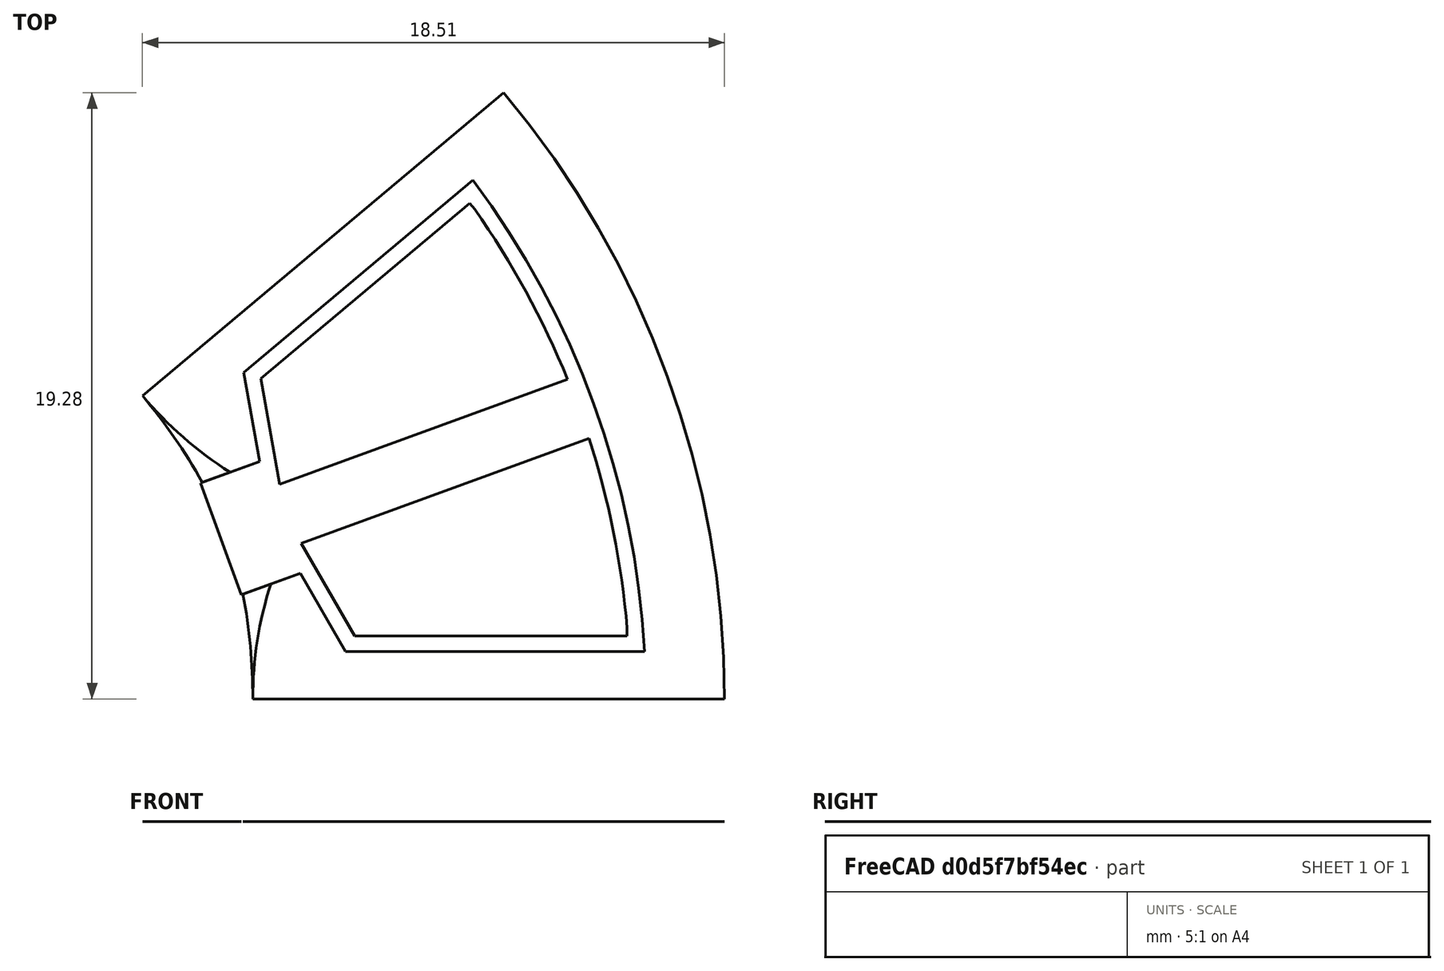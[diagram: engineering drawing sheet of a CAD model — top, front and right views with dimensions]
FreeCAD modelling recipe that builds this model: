
FCSTD DOCUMENT  (FreeCAD 0.18R4 (GitTag))
Label: StatorIRRoundBack
License: All rights reserved
LicenseURL: http://en.wikipedia.org/wiki/All_rights_reserved
objects: Sketcher::SketchObject×9, Surface::Filling×5, PartDesign::Body×2, Spreadsheet::Sheet×1
note: 16 computed .brp shape members not serialized (recipe doc carries the construction recipe); baked Part::Feature solids carry a one-line shape summary decoded from their .brp

FEATURE [Spreadsheet::Sheet] Spreadsheet  label="Variables"
  cells = A2=slotNumber; B2(slotNumber)=9; A3=outerDiameter; B3(outerDiameter)=60; A4=innerDiameter; B4(innerDiameter)=30; A5=stackLength; B5(stackLength)=20; A6=stackingFactor; B6(stackingFactor)=0.95; A7=cuttingThickness; B7(cuttingThickness)=0.1; A8=skewAngle; B8(skewAngle)=0; A9=segmentAngle; B9(segmentAngle)==360 / slotNumber; A10=tipHeightReduction; B10(tipHeightReduction)=3; A11=toothThickness; B11(toothThickness)=3; A12=yokeThickness; B12(yokeThickness)=2.5; A13=tipHeight; B13(tipHeight)=2; A14=tipAngle; B14(tipAngle)=120; A15=openingLeft; B15(openingLeft)=1.9; A16=openingRight; B16(openingRight)=1.9; A17=slotIsolation; B17(slotIsolation)=0.5; A18=windingAngle; B18(windingAngle)=35; A19=heightRatio; B19(heightRatio)=45; A20=roundingRadii; B20(roundingRadii)=0.2; A21=backWidth; B21(backWidth)=3; A22=backAngle; B22(backAngle)=90; A23=phaseSeparation; B23(phaseSeparation)=2; A24=axialOverhang; B24(axialOverhang)=1.2; A25=axialHeight; B25(axialHeight)=3
FEATURE [Sketcher::SketchObject] Sketch003  label="StatorSketch1"
  MapMode = 5
  Support = -> [XY_Plane]
  expr: Constraints[22] = Variables.openingLeft
  expr: Constraints[54] = Variables.tipHeight
  expr: Constraints[11] = Variables.innerDiameter / 2
  expr: Constraints[5] = Variables.segmentAngle
  expr: Constraints[37] = Variables.tipAngle
  expr: Constraints[30] = Variables.tipHeight
  expr: Constraints[28] = Variables.openingRight
  expr: Constraints[51] = Variables.outerDiameter / 2 - Variables.yokeThickness
  expr: Constraints[18] = Variables.segmentAngle / 2
  expr: Constraints[32] = Variables.tipHeight * (1 - Variables.tipHeightReduction / 100)
  expr: Constraints[6] = Variables.outerDiameter / 2
  expr: Constraints[48] = Variables.tipAngle
  expr: Constraints[47] = Variables.tipHeight * (1 - Variables.tipHeightReduction / 100)
  expr: Constraints[42] = Variables.toothThickness / 2
  sketch-geometry (24):
    g0: LineSegment [constr] StartX=0 StartY=0 StartZ=0 EndX=22.9813 EndY=19.2836 EndZ=0
    g1: LineSegment [constr] StartX=0 StartY=0 StartZ=0 EndX=30 EndY=0 EndZ=0
    g2: ArcOfCircle CenterX=0 CenterY=0 CenterZ=0 NormalX=0 NormalY=0 NormalZ=1 AngleXU=0 Radius=30 StartAngle=0 EndAngle=0.698132
    g3: ArcOfCircle [constr] CenterX=0 CenterY=0 CenterZ=0 NormalX=0 NormalY=0 NormalZ=1 AngleXU=0 Radius=15 StartAngle=0 EndAngle=0.698132
    g4: LineSegment [constr] StartX=13.3338 StartY=6.87098 StartZ=0 EndX=27.4859 EndY=12.0219 EndZ=0
    g5: LineSegment [constr] StartX=14.6308 StartY=3.30731 StartZ=0 EndX=28.7829 EndY=8.45826 EndZ=0
    g6: LineSegment [constr] StartX=28.1908 StartY=10.2606 StartZ=0 EndX=14.0954 EndY=5.1303 EndZ=0
    g7: LineSegment [constr] StartX=0 StartY=0 StartZ=0 EndX=14.0954 EndY=5.1303 EndZ=0
    g8: LineSegment [constr] StartX=13.3338 StartY=6.87098 StartZ=0 EndX=14.0954 EndY=5.1303 EndZ=0
    g9: LineSegment [constr] StartX=14.0954 StartY=5.1303 StartZ=0 EndX=14.6308 EndY=3.30731 EndZ=0
    g10: LineSegment [constr] StartX=13.3902 StartY=6.8915 StartZ=0 EndX=15.2132 EndY=7.55502 EndZ=0
    g11: LineSegment StartX=13.3902 StartY=6.8915 StartZ=0 EndX=15.2132 EndY=7.55502 EndZ=0
    g12: LineSegment StartX=15.2132 StartY=7.55502 StartZ=0 EndX=14.7136 EndY=10.3881 EndZ=0
    g13: LineSegment StartX=14.7136 StartY=10.3881 StartZ=0 EndX=21.999 EndY=16.5013 EndZ=0
    g14: LineSegment [constr] StartX=14.7136 StartY=10.3881 StartZ=0 EndX=13.7494 EndY=11.5371 EndZ=0
    g15: LineSegment StartX=27.4591 StartY=1.5 StartZ=0 EndX=17.9486 EndY=1.5 EndZ=0
    g16: LineSegment StartX=17.9486 StartY=1.5 StartZ=0 EndX=16.5102 EndY=3.99135 EndZ=0
    g17: LineSegment StartX=16.5102 StartY=3.99135 StartZ=0 EndX=14.6872 EndY=3.32784 EndZ=0
    g18: LineSegment [constr] StartX=27.4591 StartY=1.5 StartZ=0 EndX=27.4591 EndY=0 EndZ=0
    g19: LineSegment StartX=11.4907 StartY=9.64181 StartZ=0 EndX=22.9813 EndY=19.2836 EndZ=0
    g20: LineSegment StartX=30 StartY=0 StartZ=0 EndX=15 EndY=0 EndZ=0
    g21: ArcOfCircle CenterX=-2.86017 CenterY=0 CenterZ=0 NormalX=0 NormalY=0 NormalZ=1 AngleXU=0 Radius=17.8602 StartAngle=0 EndAngle=0.187423
    g22: ArcOfCircle CenterX=-2.19102 CenterY=-1.83848 CenterZ=0 NormalX=0 NormalY=0 NormalZ=1 AngleXU=0 Radius=17.8602 StartAngle=0.510709 EndAngle=0.698132
    g23: ArcOfCircle CenterX=0 CenterY=0 CenterZ=0 NormalX=0 NormalY=0 NormalZ=1 AngleXU=0 Radius=27.5 StartAngle=0.0545725 EndAngle=0.643559
  constraints (69):
    c: Angle(g-1,g1) = 0
    c: Coincident(g0,g-1)
    c: Coincident(g1,g-1)
    c: Coincident(g2,g-1)
    c: Coincident(g2,g0)
    c: Angle(g1,g0) = 0.698132
    c: Radius(g2) = 30
    c: Coincident(g2,g1)
    c: Coincident(g3,g-1)
    c: PointOnObject(g3,g1)
    c: PointOnObject(g3,g0)
    c: Radius(g3) = 15
    c: PointOnObject(g4,g3)
    c: PointOnObject(g4,g2)
    c: PointOnObject(g5,g3)
    c: PointOnObject(g5,g2)
    c: PointOnObject(g6,g2)
    c: PointOnObject(g6,g3)
    c: Angle(g1,g6) = 0.349066
    c: Coincident(g7,g-1)
    c: Coincident(g7,g6)
    c: Coincident(g8,g4)
    c: Distance(g8) = 1.9
    c: Coincident(g8,g6)
    c: Parallel(g4,g6)
    c: Parallel(g5,g6)
    c: Coincident(g9,g6)
    c: Coincident(g9,g5)
    c: Distance(g9) = 1.9
    c: PointOnObject(g10,g4)
    c: Distance(g4,g10) = 2
    c: Angle(g4,g10) = 3.14159
    c: Distance(g10,g10) = 1.94
    c: Coincident(g11,g10)
    c: Coincident(g12,g11)
    c: Coincident(g13,g12)
    c: Coincident(g11,g10)
    c: Angle(g12,g13) = 2.0944
    c: Parallel(g0,g13)
    c: Coincident(g14,g12)
    c: PointOnObject(g14,g0)
    c: Angle(g13,g14) = 1.5708
    c: Distance(g14) = 1.5
    c: Coincident(g16,g15)
    c: PointOnObject(g16,g5)
    c: Coincident(g17,g16)
    c: PointOnObject(g17,g5)
    c: Distance(g17) = 1.94
    c: Angle(g15,g16) = 2.0944
    c: Parallel(g15,g1)
    c: Symmetric(g23,g23,g6)
    c: Distance(g-1,g23) = 27.5
    c: PointOnObject(g18,g1)
    c: Vertical(g18)
    c: Distance(g5,g16) = 2
    c: Coincident(g19,g3)
    c: Coincident(g19,g0)
    c: Coincident(g20,g2)
    c: Coincident(g20,g3)
    c: PointOnObject(g21,g-1)
    c: Coincident(g21,g17)
    c: Coincident(g21,g20)
    c: PointOnObject(g22,g0)
    c: Coincident(g22,g11)
    c: Coincident(g22,g19)
    c: Coincident(g23,g2)
    c: Coincident(g23,g13)
    c: Coincident(g15,g23)
    c: Coincident(g18,g15)
FEATURE [Sketcher::SketchObject] Sketch  label="StatorStack"
  MapMode = 5
  Support = -> [XY_Plane001]
  expr: Constraints[20] = Variables.innerDiameter / 2
  expr: Constraints[10] = Variables.outerDiameter / 2
  expr: Constraints[9] = Variables.innerDiameter / 2
  expr: Constraints[8] = Variables.stackLength
  sketch-geometry (8):
    g0: LineSegment StartX=-10 StartY=15 StartZ=0 EndX=10 EndY=15 EndZ=0
    g1: LineSegment StartX=10 StartY=15 StartZ=0 EndX=10 EndY=30 EndZ=0
    g2: LineSegment StartX=10 StartY=30 StartZ=0 EndX=-10 EndY=30 EndZ=0
    g3: LineSegment StartX=-10 StartY=30 StartZ=0 EndX=-10 EndY=15 EndZ=0
    g4: LineSegment StartX=-10 StartY=-15 StartZ=0 EndX=10 EndY=-15 EndZ=0
    g5: LineSegment StartX=10 StartY=-15 StartZ=0 EndX=10 EndY=-30 EndZ=0
    g6: LineSegment StartX=10 StartY=-30 StartZ=0 EndX=-10 EndY=-30 EndZ=0
    g7: LineSegment StartX=-10 StartY=-30 StartZ=0 EndX=-10 EndY=-15 EndZ=0
  constraints (22):
    c: Coincident(g0,g1)
    c: Coincident(g1,g2)
    c: Coincident(g2,g3)
    c: Coincident(g3,g0)
    c: Horizontal(g2)
    c: Vertical(g1)
    c: Vertical(g3)
    c: Symmetric(g0,g0,g-2)
    c: DistanceX(g0,g0) = 20
    c: DistanceY(g-1,g0) = 15
    c: DistanceY(g-1,g1) = 30
    c: Coincident(g4,g5)
    c: Coincident(g5,g6)
    c: Coincident(g6,g7)
    c: Coincident(g7,g4)
    c: Horizontal(g6)
    c: Vertical(g5)
    c: Vertical(g7)
    c: Equal(g4,g0)
    c: Symmetric(g4,g4,g-2)
    c: DistanceY(g4,g-1) = 15
    c: Equal(g7,g3)
FEATURE [Sketcher::SketchObject] Sketch008  label="SlotSketch"
  MapMode = 5
  Support = -> [XY_Plane]
  expr: Constraints[63] = Variables.outerDiameter / 2 - Variables.yokeThickness
  expr: Constraints[43] = Variables.toothThickness / 2
  expr: Constraints[34] = Variables.toothThickness / 2
  expr: Constraints[40] = Variables.outerDiameter / 2 - Variables.yokeThickness
  expr: Constraints[21] = Variables.openingLeft
  expr: Constraints[44] = Variables.tipHeight
  expr: Constraints[57] = Variables.backWidth
  expr: Constraints[5] = Variables.segmentAngle
  expr: Constraints[29] = Variables.tipAngle
  expr: Constraints[27] = Variables.openingRight
  expr: Constraints[62] = Variables.segmentAngle / 2
  expr: Constraints[6] = Variables.outerDiameter / 2
  expr: Constraints[37] = Variables.tipAngle
  expr: Constraints[11] = Variables.innerDiameter / 2
  sketch-geometry (23):
    g0: LineSegment [constr] StartX=0 StartY=0 StartZ=0 EndX=22.9813 EndY=19.2836 EndZ=0
    g1: LineSegment [constr] StartX=0 StartY=0 StartZ=0 EndX=30 EndY=0 EndZ=0
    g2: ArcOfCircle [constr] CenterX=0 CenterY=0 CenterZ=0 NormalX=0 NormalY=0 NormalZ=1 AngleXU=0 Radius=30 StartAngle=0 EndAngle=0.698132
    g3: ArcOfCircle [constr] CenterX=0 CenterY=0 CenterZ=0 NormalX=0 NormalY=0 NormalZ=1 AngleXU=0 Radius=15 StartAngle=0 EndAngle=0.698132
    g4: LineSegment [constr] StartX=13.3338 StartY=6.87098 StartZ=0 EndX=27.4859 EndY=12.0219 EndZ=0
    g5: LineSegment [constr] StartX=14.6308 StartY=3.30731 StartZ=0 EndX=28.7829 EndY=8.45826 EndZ=0
    g6: LineSegment [constr] StartX=28.1908 StartY=10.2606 StartZ=0 EndX=14.0954 EndY=5.1303 EndZ=0
    g7: LineSegment [constr] StartX=0 StartY=0 StartZ=0 EndX=14.0954 EndY=5.1303 EndZ=0
    g8: LineSegment [constr] StartX=13.3338 StartY=6.87098 StartZ=0 EndX=14.0954 EndY=5.1303 EndZ=0
    g9: LineSegment [constr] StartX=14.0954 StartY=5.1303 StartZ=0 EndX=14.6308 EndY=3.30731 EndZ=0
    g10: LineSegment StartX=15.2132 StartY=7.55502 StartZ=0 EndX=14.7136 EndY=10.3881 EndZ=0
    g11: LineSegment StartX=14.7136 StartY=10.3881 StartZ=0 EndX=21.999 EndY=16.5013 EndZ=0
    g12: LineSegment [constr] StartX=14.7136 StartY=10.3881 StartZ=0 EndX=13.7494 EndY=11.5371 EndZ=0
    g13: LineSegment [constr] StartX=25.29 StartY=10.8011 StartZ=0 EndX=26.3161 EndY=7.98201 EndZ=0
    g14: LineSegment StartX=27.4591 StartY=1.5 StartZ=0 EndX=17.9486 EndY=1.5 EndZ=0
    g15: LineSegment StartX=17.9486 StartY=1.5 StartZ=0 EndX=16.5102 EndY=3.99135 EndZ=0
    g16: LineSegment [constr] StartX=27.4591 StartY=1.5 StartZ=0 EndX=27.4591 EndY=0 EndZ=0
    g17: LineSegment [constr] StartX=11.4907 StartY=9.64181 StartZ=0 EndX=22.9813 EndY=19.2836 EndZ=0
    g18: LineSegment [constr] StartX=30 StartY=0 StartZ=0 EndX=15 EndY=0 EndZ=0
    g19: LineSegment StartX=13.3338 StartY=6.87098 StartZ=0 EndX=14.6308 EndY=3.30731 EndZ=0
    g20: LineSegment StartX=13.3338 StartY=6.87098 StartZ=0 EndX=15.2132 EndY=7.55502 EndZ=0
    g21: LineSegment StartX=14.6308 StartY=3.30731 StartZ=0 EndX=16.5102 EndY=3.99135 EndZ=0
    g22: ArcOfCircle CenterX=0 CenterY=0 CenterZ=0 NormalX=0 NormalY=0 NormalZ=1 AngleXU=0 Radius=27.5 StartAngle=0.0545725 EndAngle=0.643559
  constraints (64):
    c: Angle(g-1,g1) = 0
    c: Coincident(g0,g-1)
    c: Coincident(g1,g-1)
    c: Coincident(g2,g-1)
    c: Coincident(g2,g0)
    c: Angle(g1,g0) = 0.698132
    c: Radius(g2) = 30
    c: Coincident(g2,g1)
    c: Coincident(g3,g-1)
    c: PointOnObject(g3,g1)
    c: PointOnObject(g3,g0)
    c: Radius(g3) = 15
    c: PointOnObject(g4,g3)
    c: PointOnObject(g4,g2)
    c: PointOnObject(g5,g3)
    c: PointOnObject(g5,g2)
    c: PointOnObject(g6,g2)
    c: PointOnObject(g6,g3)
    c: Coincident(g7,g-1)
    c: Coincident(g7,g6)
    c: Coincident(g8,g4)
    c: Distance(g8) = 1.9
    c: Coincident(g8,g6)
    c: Parallel(g4,g6)
    c: Parallel(g5,g6)
    c: Coincident(g9,g6)
    c: Coincident(g9,g5)
    c: Distance(g9) = 1.9
    c: Coincident(g11,g10)
    c: Angle(g10,g11) = 2.0944
    c: Parallel(g0,g11)
    c: Coincident(g12,g10)
    c: PointOnObject(g12,g0)
    c: Angle(g11,g12) = 1.5708
    c: Distance(g12) = 1.5
    c: Coincident(g15,g14)
    c: PointOnObject(g15,g5)
    c: Angle(g14,g15) = 2.0944
    c: Parallel(g14,g1)
    c: Symmetric(g13,g13,g6)
    c: Distance(g-1,g13) = 27.5
    c: PointOnObject(g16,g1)
    c: Vertical(g16)
    c: DistanceY(g16,g16) = 1.5
    c: Distance(g5,g15) = 2
    c: Coincident(g17,g3)
    c: Coincident(g17,g0)
    c: Coincident(g18,g2)
    c: Coincident(g18,g3)
    c: Symmetric(g15,g10,g6)
    c: Coincident(g19,g4)
    c: Coincident(g19,g5)
    c: Coincident(g20,g19)
    c: Coincident(g20,g10)
    c: Coincident(g21,g19)
    c: Coincident(g21,g15)
    c: Coincident(g22,g-1)
    c: Distance(g13) = 3
    c: Coincident(g22,g11)
    c: Coincident(g22,g14)
    c: Coincident(g14,g16)
    c: Parallel(g7,g6)
    c: Angle(g1,g7) = 0.349066
    c: Radius(g22) = 27.5
FEATURE [Surface::Filling] Surface  label="SlotSketch_Surface"
  Anisotropy = false
  BoundaryEdges = -> [Sketch008]
  BoundaryOrder = [0,0,0,0,0,0,0,0]
  Degree = 3
  Iterations = 2
  MaximumDegree = 8
  MaximumSegments = 9
  PointsOnCurve = 15
  TolAngular = 0.01
  TolCurvature = 0.1
  Tolerance2d = 1e-05
  Tolerance3d = 0.0001
FEATURE [Surface::Filling] Surface002  label="StatorSketch1_Surface"
  Anisotropy = false
  BoundaryEdges = -> [Sketch003]
  BoundaryOrder = [0,0,0,0,0,0,0,0,0,0,0,0]
  Degree = 3
  Iterations = 2
  MaximumDegree = 8
  MaximumSegments = 9
  PointsOnCurve = 15
  TolAngular = 0.01
  TolCurvature = 0.1
  Tolerance2d = 1e-05
  Tolerance3d = 0.0001
FEATURE [Sketcher::SketchObject] Sketch010  label="ToothLine"
  ExternalGeometry = -> [Sketch008]
  MapMode = 5
  Support = -> [XY_Plane]
  expr: Constraints[0] = Variables.toothThickness
  sketch-geometry (1):
    g0: LineSegment StartX=18.3563 StartY=13.4447 StartZ=0 EndX=16.428 EndY=15.7428 EndZ=0
  constraints (3):
    c: Distance(g0) = 3
    c: Symmetric(g-3,g-3,g0)
    c: Angle(g-3,g0) = 1.5708
FEATURE [Sketcher::SketchObject] Sketch011  label="YokeLine"
  ExternalGeometry = -> [Sketch008]
  MapMode = 5
  Support = -> [XY_Plane]
  expr: Constraints[0] = Variables.yokeThickness
  sketch-geometry (3):
    g0: LineSegment StartX=25.8415 StartY=9.40555 StartZ=0 EndX=28.1908 EndY=10.2606 EndZ=0
    g1: LineSegment [constr] StartX=21.999 StartY=16.5013 StartZ=0 EndX=27.4591 EndY=1.5 EndZ=0
    g2: LineSegment [constr] StartX=25.8415 StartY=9.40555 StartZ=0 EndX=24.7291 EndY=9.00064 EndZ=0
  constraints (8):
    c: Distance(g0) = 2.5
    c: PointOnObject(g0,g-3)
    c: Coincident(g1,g-3)
    c: Coincident(g1,g-3)
    c: Coincident(g2,g0)
    c: Angle(g2,g0) = 3.14159
    c: Angle(g1,g2) = 1.5708
    c: Symmetric(g1,g1,g2)
FEATURE [Sketcher::SketchObject] Sketch012  label="StatorSketch2"
  MapMode = 5
  Support = -> [XY_Plane]
  expr: Constraints[22] = Variables.openingLeft
  expr: Constraints[54] = Variables.tipHeight
  expr: Constraints[11] = Variables.innerDiameter / 2
  expr: Constraints[5] = Variables.segmentAngle
  expr: Constraints[37] = Variables.tipAngle
  expr: Constraints[30] = Variables.tipHeight
  expr: Constraints[28] = Variables.openingRight
  expr: Constraints[51] = Variables.outerDiameter / 2 - Variables.yokeThickness
  expr: Constraints[18] = Variables.segmentAngle / 2
  expr: Constraints[32] = Variables.tipHeight * (1 - Variables.tipHeightReduction / 100)
  expr: Constraints[6] = Variables.outerDiameter / 2
  expr: Constraints[48] = Variables.tipAngle
  expr: Constraints[47] = Variables.tipHeight * (1 - Variables.tipHeightReduction / 100)
  expr: Constraints[42] = Variables.toothThickness / 2
  sketch-geometry (24):
    g0: LineSegment [constr] StartX=0 StartY=0 StartZ=0 EndX=22.9813 EndY=19.2836 EndZ=0
    g1: LineSegment [constr] StartX=0 StartY=0 StartZ=0 EndX=30 EndY=0 EndZ=0
    g2: ArcOfCircle CenterX=0 CenterY=0 CenterZ=0 NormalX=0 NormalY=0 NormalZ=1 AngleXU=0 Radius=30 StartAngle=0 EndAngle=0.698132
    g3: ArcOfCircle [constr] CenterX=0 CenterY=0 CenterZ=0 NormalX=0 NormalY=0 NormalZ=1 AngleXU=0 Radius=15 StartAngle=0 EndAngle=0.698132
    g4: LineSegment [constr] StartX=13.3338 StartY=6.87098 StartZ=0 EndX=27.4859 EndY=12.0219 EndZ=0
    g5: LineSegment [constr] StartX=14.6308 StartY=3.30731 StartZ=0 EndX=28.7829 EndY=8.45826 EndZ=0
    g6: LineSegment [constr] StartX=28.1908 StartY=10.2606 StartZ=0 EndX=14.0954 EndY=5.1303 EndZ=0
    g7: LineSegment [constr] StartX=0 StartY=0 StartZ=0 EndX=14.0954 EndY=5.1303 EndZ=0
    g8: LineSegment [constr] StartX=13.3338 StartY=6.87098 StartZ=0 EndX=14.0954 EndY=5.1303 EndZ=0
    g9: LineSegment [constr] StartX=14.0954 StartY=5.1303 StartZ=0 EndX=14.6308 EndY=3.30731 EndZ=0
    g10: LineSegment [constr] StartX=14.2735 StartY=7.213 StartZ=0 EndX=15.2132 EndY=7.55502 EndZ=0
    g11: LineSegment StartX=14.2735 StartY=7.213 StartZ=0 EndX=15.2132 EndY=7.55502 EndZ=0
    g12: LineSegment StartX=15.2132 StartY=7.55502 StartZ=0 EndX=14.7136 EndY=10.3881 EndZ=0
    g13: LineSegment StartX=14.7136 StartY=10.3881 StartZ=0 EndX=21.999 EndY=16.5013 EndZ=0
    g14: LineSegment [constr] StartX=14.7136 StartY=10.3881 StartZ=0 EndX=13.7494 EndY=11.5371 EndZ=0
    g15: LineSegment StartX=27.4591 StartY=1.5 StartZ=0 EndX=17.9486 EndY=1.5 EndZ=0
    g16: LineSegment StartX=17.9486 StartY=1.5 StartZ=0 EndX=16.5102 EndY=3.99135 EndZ=0
    g17: LineSegment StartX=16.5102 StartY=3.99135 StartZ=0 EndX=15.5705 EndY=3.64933 EndZ=0
    g18: LineSegment [constr] StartX=27.4591 StartY=1.5 StartZ=0 EndX=27.4591 EndY=0 EndZ=0
    g19: LineSegment StartX=11.4907 StartY=9.64181 StartZ=0 EndX=22.9813 EndY=19.2836 EndZ=0
    g20: LineSegment StartX=30 StartY=0 StartZ=0 EndX=15 EndY=0 EndZ=0
    g21: ArcOfCircle CenterX=0 CenterY=0 CenterZ=0 NormalX=0 NormalY=0 NormalZ=1 AngleXU=0 Radius=27.5 StartAngle=0.0545725 EndAngle=0.643559
    g22: ArcOfCircle CenterX=20.6498 CenterY=17.3272 CenterZ=0 NormalX=0 NormalY=0 NormalZ=1 AngleXU=0 Radius=11.9564 StartAngle=3.83972 EndAngle=4.14989
    g23: ArcOfCircle CenterX=26.9564 CenterY=0 CenterZ=0 NormalX=0 NormalY=0 NormalZ=1 AngleXU=0 Radius=11.9564 StartAngle=2.83142 EndAngle=3.14159
  constraints (69):
    c: Angle(g-1,g1) = 0
    c: Coincident(g0,g-1)
    c: Coincident(g1,g-1)
    c: Coincident(g2,g-1)
    c: Coincident(g2,g0)
    c: Angle(g1,g0) = 0.698132
    c: Radius(g2) = 30
    c: Coincident(g2,g1)
    c: Coincident(g3,g-1)
    c: PointOnObject(g3,g1)
    c: PointOnObject(g3,g0)
    c: Radius(g3) = 15
    c: PointOnObject(g4,g3)
    c: PointOnObject(g4,g2)
    c: PointOnObject(g5,g3)
    c: PointOnObject(g5,g2)
    c: PointOnObject(g6,g2)
    c: PointOnObject(g6,g3)
    c: Angle(g1,g6) = 0.349066
    c: Coincident(g7,g-1)
    c: Coincident(g7,g6)
    c: Coincident(g8,g4)
    c: Distance(g8) = 1.9
    c: Coincident(g8,g6)
    c: Parallel(g4,g6)
    c: Parallel(g5,g6)
    c: Coincident(g9,g6)
    c: Coincident(g9,g5)
    c: Distance(g9) = 1.9
    c: PointOnObject(g10,g4)
    c: Distance(g4,g10) = 2
    c: Angle(g4,g10) = 3.14159
    c: Distance(g10,g10) = 1.94
    c: Coincident(g11,g10)
    c: Coincident(g12,g11)
    c: Coincident(g13,g12)
    c: Coincident(g11,g10)
    c: Angle(g12,g13) = 2.0944
    c: Parallel(g0,g13)
    c: Coincident(g14,g12)
    c: PointOnObject(g14,g0)
    c: Angle(g13,g14) = 1.5708
    c: Distance(g14) = 1.5
    c: Coincident(g16,g15)
    c: PointOnObject(g16,g5)
    c: Coincident(g17,g16)
    c: PointOnObject(g17,g5)
    c: Distance(g17) = 1.94
    c: Angle(g15,g16) = 2.0944
    c: Parallel(g15,g1)
    c: Symmetric(g21,g21,g6)
    c: Distance(g-1,g21) = 27.5
    c: PointOnObject(g18,g1)
    c: Vertical(g18)
    c: Distance(g5,g16) = 2
    c: Coincident(g19,g3)
    c: Coincident(g19,g0)
    c: Coincident(g20,g2)
    c: Coincident(g20,g3)
    c: Coincident(g21,g2)
    c: Coincident(g21,g13)
    c: Coincident(g15,g21)
    c: Coincident(g18,g15)
    c: PointOnObject(g22,g19)
    c: Coincident(g22,g19)
    c: Coincident(g22,g11)
    c: PointOnObject(g23,g20)
    c: Coincident(g23,g20)
    c: Coincident(g23,g17)
FEATURE [Surface::Filling] Surface001  label="StatorSketch2_Surface"
  Anisotropy = false
  BoundaryEdges = -> [Sketch012]
  BoundaryOrder = [0,0,0,0,0,0,0,0,0,0,0,0,0,0]
  Degree = 3
  Iterations = 2
  MaximumDegree = 8
  MaximumSegments = 9
  PointsOnCurve = 15
  TolAngular = 0.01
  TolCurvature = 0.1
  Tolerance2d = 1e-05
  Tolerance3d = 0.0001
FEATURE [Sketcher::SketchObject] Sketch013  label="TerminalLeftSketch"
  ExternalGeometry = -> [Sketch008]
  MapMode = 5
  Support = -> [XY_Plane]
  expr: Constraints[19] = Variables.slotIsolation
  expr: Constraints[20] = Variables.slotIsolation / 2
  expr: Constraints[15] = Variables.outerDiameter / 2 - Variables.yokeThickness - Variables.slotIsolation
  expr: Constraints[12] = Variables.phaseSeparation / 2
  sketch-geometry (9):
    g0: LineSegment StartX=22.0575 StartY=15.5713 StartZ=0 EndX=21.8968 EndY=15.7628 EndZ=0
    g1: LineSegment StartX=21.8968 StartY=15.7628 StartZ=0 EndX=15.2562 EndY=10.1906 EndZ=0
    g2: LineSegment StartX=15.2562 StartY=10.1906 StartZ=0 EndX=15.8483 EndY=6.83248 EndZ=0
    g3: LineSegment StartX=15.8483 StartY=6.83248 StartZ=0 EndX=25.0123 EndY=10.1679 EndZ=0
    g4: ArcOfCircle CenterX=0 CenterY=0 CenterZ=0 NormalX=0 NormalY=0 NormalZ=1 AngleXU=0 Radius=27 StartAngle=0.386111 EndAngle=0.614702
    g5: LineSegment [constr] StartX=0 StartY=0 StartZ=0 EndX=15.8617 EndY=5.77319 EndZ=0
    g6: LineSegment [constr] StartX=16.1903 StartY=5.89279 StartZ=0 EndX=15.8483 EndY=6.83248 EndZ=0
    g7: LineSegment [constr] StartX=21.8968 StartY=15.7628 StartZ=0 EndX=21.5754 EndY=16.1458 EndZ=0
    g8: LineSegment [constr] StartX=15.2562 StartY=10.1906 StartZ=0 EndX=14.7637 EndY=10.1038 EndZ=0
  constraints (26):
    c: Coincident(g1,g0)
    c: Coincident(g2,g1)
    c: Coincident(g3,g2)
    c: Coincident(g4,g-1)
    c: Coincident(g4,g3)
    c: Coincident(g4,g0)
    c: Coincident(g5,g4)
    c: Symmetric(g-5,g-6,g5)
    c: Parallel(g3,g5)
    c: PointOnObject(g6,g5)
    c: Coincident(g6,g2)
    c: Angle(g6,g5) = 1.5708
    c: Distance(g6) = 1
    c: Parallel(g2,g-5)
    c: Parallel(g1,g-4)
    c: Radius(g4) = 27
    c: Coincident(g7,g0)
    c: PointOnObject(g7,g-4)
    c: Angle(g7,g1) = 1.5708
    c: Distance(g7) = 0.5
    c: Distance(g0) = 0.25
    c: Coincident(g8,g1)
    c: PointOnObject(g8,g-5)
    c: Angle(g8,g2) = 1.5708
    c: Equal(g7,g8)
    c: Angle(g1,g0) = 1.5708
FEATURE [Surface::Filling] Surface004  label="TerminalLeftSketch_Surface"
  Anisotropy = false
  BoundaryEdges = -> [Sketch013]
  BoundaryOrder = [0,0,0,0,0]
  Degree = 3
  Iterations = 2
  MaximumDegree = 8
  MaximumSegments = 9
  PointsOnCurve = 15
  TolAngular = 0.01
  TolCurvature = 0.1
  Tolerance2d = 1e-05
  Tolerance3d = 0.0001
FEATURE [Sketcher::SketchObject] Sketch014  label="TerminalRightSketch"
  ExternalGeometry = -> [Sketch008]
  expr: Constraints[25] = Variables.slotIsolation / 2
  expr: Constraints[20] = Variables.slotIsolation
  expr: Constraints[15] = Variables.phaseSeparation / 2
  expr: Constraints[11] = Variables.outerDiameter / 2 - Variables.yokeThickness - Variables.slotIsolation
  sketch-geometry (9):
    g0: LineSegment StartX=26.9061 StartY=2.25 StartZ=0 EndX=26.9061 EndY=2 EndZ=0
    g1: LineSegment StartX=26.9061 StartY=2 StartZ=0 EndX=18.2373 EndY=2 EndZ=0
    g2: LineSegment StartX=18.2373 StartY=2 StartZ=0 EndX=16.5323 EndY=4.95309 EndZ=0
    g3: LineSegment StartX=16.5323 StartY=4.95309 StartZ=0 EndX=25.6963 EndY=8.28852 EndZ=0
    g4: ArcOfCircle CenterX=0 CenterY=0 CenterZ=0 NormalX=0 NormalY=0 NormalZ=1 AngleXU=0 Radius=27 StartAngle=0.0834301 EndAngle=0.31202
    g5: LineSegment [constr] StartX=0 StartY=0 StartZ=0 EndX=15.8617 EndY=5.77319 EndZ=0
    g6: LineSegment [constr] StartX=16.5323 StartY=4.95309 StartZ=0 EndX=16.1903 EndY=5.89279 EndZ=0
    g7: LineSegment [constr] StartX=26.9061 StartY=2 StartZ=0 EndX=26.9061 EndY=1.5 EndZ=0
    g8: LineSegment [constr] StartX=18.2373 StartY=2 StartZ=0 EndX=17.8043 EndY=1.75 EndZ=0
  constraints (26):
    c: Coincident(g1,g0)
    c: Horizontal(g1)
    c: Coincident(g2,g1)
    c: Coincident(g3,g2)
    c: Coincident(g4,g-1)
    c: Coincident(g4,g3)
    c: Coincident(g4,g0)
    c: Coincident(g5,g4)
    c: Symmetric(g-5,g-6,g5)
    c: Parallel(g3,g5)
    c: Angle(g0,g1) = 1.5708
    c: Radius(g4) = 27
    c: Coincident(g6,g2)
    c: PointOnObject(g6,g5)
    c: Angle(g5,g6) = 1.5708
    c: Distance(g6) = 1
    c: Parallel(g2,g-6)
    c: Coincident(g7,g0)
    c: PointOnObject(g7,g-7)
    c: Vertical(g7)
    c: Distance(g7) = 0.5
    c: Coincident(g8,g1)
    c: PointOnObject(g8,g-6)
    c: Angle(g2,g8) = 1.5708
    c: Equal(g7,g8)
    c: Distance(g0) = 0.25
FEATURE [PartDesign::Body] Body  label="TopView"
  Group = -> [Sketch003,Sketch008,Sketch010,Sketch011,Sketch012,Sketch013,Sketch014]
  Origin = -> Origin
FEATURE [Surface::Filling] Surface003  label="TerminalRightSketch_Surface"
  Anisotropy = false
  BoundaryEdges = -> [Sketch014]
  BoundaryOrder = [0,0,0,0,0]
  Degree = 3
  Iterations = 2
  MaximumDegree = 8
  MaximumSegments = 9
  PointsOnCurve = 15
  TolAngular = 0.01
  TolCurvature = 0.1
  Tolerance2d = 1e-05
  Tolerance3d = 0.0001
FEATURE [Sketcher::SketchObject] Sketch016  label="Isolation"
  ExternalGeometry = -> [Sketch]
  MapMode = 5
  Support = -> [XY_Plane001]
  expr: Constraints[83] = Variables.axialHeight / 2
  expr: Constraints[19] = (Variables.outerDiameter - Variables.innerDiameter) / 2 - Variables.yokeThickness - Variables.tipHeight
  expr: Constraints[18] = Variables.yokeThickness
  expr: Constraints[17] = Variables.tipHeight
  expr: Constraints[16] = Variables.axialHeight
  expr: Constraints[15] = Variables.axialHeight + Variables.axialOverhang
  sketch-geometry (32):
    g0: LineSegment StartX=-10 StartY=30 StartZ=0 EndX=-10 EndY=15 EndZ=0
    g1: LineSegment StartX=-10 StartY=15 StartZ=0 EndX=-12.7 EndY=15 EndZ=0
    g2: LineSegment StartX=-12.7 StartY=15 StartZ=0 EndX=-12.7 EndY=17 EndZ=0
    g3: LineSegment StartX=-12.7 StartY=17 StartZ=0 EndX=-11.2 EndY=17 EndZ=0
    g4: LineSegment StartX=-11.2 StartY=17 StartZ=0 EndX=-11.2 EndY=27.5 EndZ=0
    g5: LineSegment StartX=-11.2 StartY=27.5 StartZ=0 EndX=-14.2 EndY=27.5 EndZ=0
    g6: LineSegment StartX=-14.2 StartY=27.5 StartZ=0 EndX=-14.2 EndY=30 EndZ=0
    g7: LineSegment StartX=-14.2 StartY=30 StartZ=0 EndX=-10 EndY=30 EndZ=0
    g8: LineSegment StartX=-12.7 StartY=-15 StartZ=0 EndX=-10 EndY=-15 EndZ=0
    g9: LineSegment StartX=-10 StartY=-15 StartZ=0 EndX=-10 EndY=-30 EndZ=0
    g10: LineSegment StartX=-10 StartY=-30 StartZ=0 EndX=-14.2 EndY=-30 EndZ=0
    g11: LineSegment StartX=-14.2 StartY=-30 StartZ=0 EndX=-14.2 EndY=-27.5 EndZ=0
    g12: LineSegment StartX=-14.2 StartY=-27.5 StartZ=0 EndX=-11.2 EndY=-27.5 EndZ=0
    g13: LineSegment StartX=-11.2 StartY=-27.5 StartZ=0 EndX=-11.2 EndY=-17 EndZ=0
    g14: LineSegment StartX=-11.2 StartY=-17 StartZ=0 EndX=-12.7 EndY=-17 EndZ=0
    g15: LineSegment StartX=-12.7 StartY=-17 StartZ=0 EndX=-12.7 EndY=-15 EndZ=0
    g16: LineSegment StartX=14.2 StartY=30 StartZ=0 EndX=10 EndY=30 EndZ=0
    g17: LineSegment StartX=10 StartY=30 StartZ=0 EndX=10 EndY=15 EndZ=0
    g18: LineSegment StartX=10 StartY=15 StartZ=0 EndX=12.7 EndY=15 EndZ=0
    g19: LineSegment StartX=12.7 StartY=15 StartZ=0 EndX=12.7 EndY=17 EndZ=0
    g20: LineSegment StartX=12.7 StartY=17 StartZ=0 EndX=11.2 EndY=17 EndZ=0
    g21: LineSegment StartX=11.2 StartY=17 StartZ=0 EndX=11.2 EndY=27.5 EndZ=0
    g22: LineSegment StartX=11.2 StartY=27.5 StartZ=0 EndX=14.2 EndY=27.5 EndZ=0
    g23: LineSegment StartX=14.2 StartY=27.5 StartZ=0 EndX=14.2 EndY=30 EndZ=0
    g24: LineSegment StartX=12.7 StartY=-15 StartZ=0 EndX=10 EndY=-15 EndZ=0
    g25: LineSegment StartX=10 StartY=-15 StartZ=0 EndX=10 EndY=-30 EndZ=0
    g26: LineSegment StartX=10 StartY=-30 StartZ=0 EndX=14.2 EndY=-30 EndZ=0
    g27: LineSegment StartX=14.2 StartY=-30 StartZ=0 EndX=14.2 EndY=-27.5 EndZ=0
    g28: LineSegment StartX=14.2 StartY=-27.5 StartZ=0 EndX=11.2 EndY=-27.5 EndZ=0
    g29: LineSegment StartX=11.2 StartY=-27.5 StartZ=0 EndX=11.2 EndY=-17 EndZ=0
    g30: LineSegment StartX=11.2 StartY=-17 StartZ=0 EndX=12.7 EndY=-17 EndZ=0
    g31: LineSegment StartX=12.7 StartY=-17 StartZ=0 EndX=12.7 EndY=-15 EndZ=0
  constraints (92):
    c: Vertical(g0)
    c: Coincident(g1,g0)
    c: Horizontal(g1)
    c: Coincident(g2,g1)
    c: Vertical(g2)
    c: Coincident(g3,g2)
    c: Horizontal(g3)
    c: Coincident(g4,g3)
    c: Vertical(g4)
    c: Coincident(g5,g4)
    c: Horizontal(g5)
    c: Coincident(g7,g6)
    c: Coincident(g7,g0)
    c: Horizontal(g7)
    c: Coincident(g6,g5)
    c: DistanceX(g7,g7) = 4.2
    c: DistanceX(g5,g5) = 3
    c: DistanceY(g2,g2) = 2
    c: DistanceY(g6,g6) = 2.5
    c: DistanceY(g4,g4) = 10.5
    c: Coincident(g0,g-6)
    c: Coincident(g8,g9)
    c: Vertical(g9)
    c: Coincident(g9,g10)
    c: Coincident(g10,g11)
    c: Coincident(g11,g12)
    c: Coincident(g12,g13)
    c: Vertical(g13)
    c: Coincident(g13,g14)
    c: Coincident(g14,g15)
    c: Coincident(g15,g8)
    c: Equal(g7,g10)
    c: Vertical(g11)
    c: Equal(g13,g4)
    c: Equal(g9,g0)
    c: Equal(g11,g6)
    c: Coincident(g8,g-4)
    c: Coincident(g16,g17)
    c: Vertical(g17)
    c: Coincident(g17,g18)
    c: Coincident(g18,g19)
    c: Vertical(g19)
    c: Coincident(g19,g20)
    c: Coincident(g20,g21)
    c: Vertical(g21)
    c: Coincident(g21,g22)
    c: Coincident(g22,g23)
    c: Coincident(g23,g16)
    c: Vertical(g23)
    c: Equal(g0,g17)
    c: Equal(g16,g7)
    c: Equal(g2,g19)
    c: Equal(g6,g23)
    c: Coincident(g-3,g16)
    c: Coincident(g24,g25)
    c: Vertical(g25)
    c: Coincident(g25,g26)
    c: Coincident(g26,g27)
    c: Vertical(g27)
    c: Coincident(g27,g28)
    c: Coincident(g28,g29)
    c: Vertical(g29)
    c: Coincident(g29,g30)
    c: Coincident(g30,g31)
    c: Coincident(g31,g24)
    c: Equal(g8,g24)
    c: Equal(g10,g26)
    c: Equal(g11,g27)
    c: Equal(g15,g31)
    c: Equal(g9,g25)
    c: Coincident(g24,g-5)
    c: Angle(g17,g16) = 1.5708
    c: Angle(g21,g22) = 1.5708
    c: Angle(g18,g17) = 1.5708
    c: Angle(g20,g21) = 1.5708
    c: Angle(g25,g24) = 1.5708
    c: Angle(g29,g30) = 1.5708
    c: Angle(g28,g29) = 1.5708
    c: Angle(g26,g25) = 1.5708
    c: Angle(g14,g13) = 1.5708
    c: Angle(g13,g12) = 1.5708
    c: Angle(g9,g10) = 1.5708
    c: Angle(g8,g9) = 1.5708
    c: DistanceX(g3,g3) = 1.5
    c: Angle(g6,g7) = 1.5708
    c: Equal(g20,g3)
    c: Equal(g3,g14)
    c: Angle(g15,g8) = 1.5708
    c: Equal(g12,g5)
    c: Equal(g28,g5)
    c: Equal(g5,g22)
    c: Angle(g24,g31) = 1.5708
FEATURE [PartDesign::Body] Body001  label="SideView"
  Group = -> [Sketch,Sketch016]
  Origin = -> Origin001
